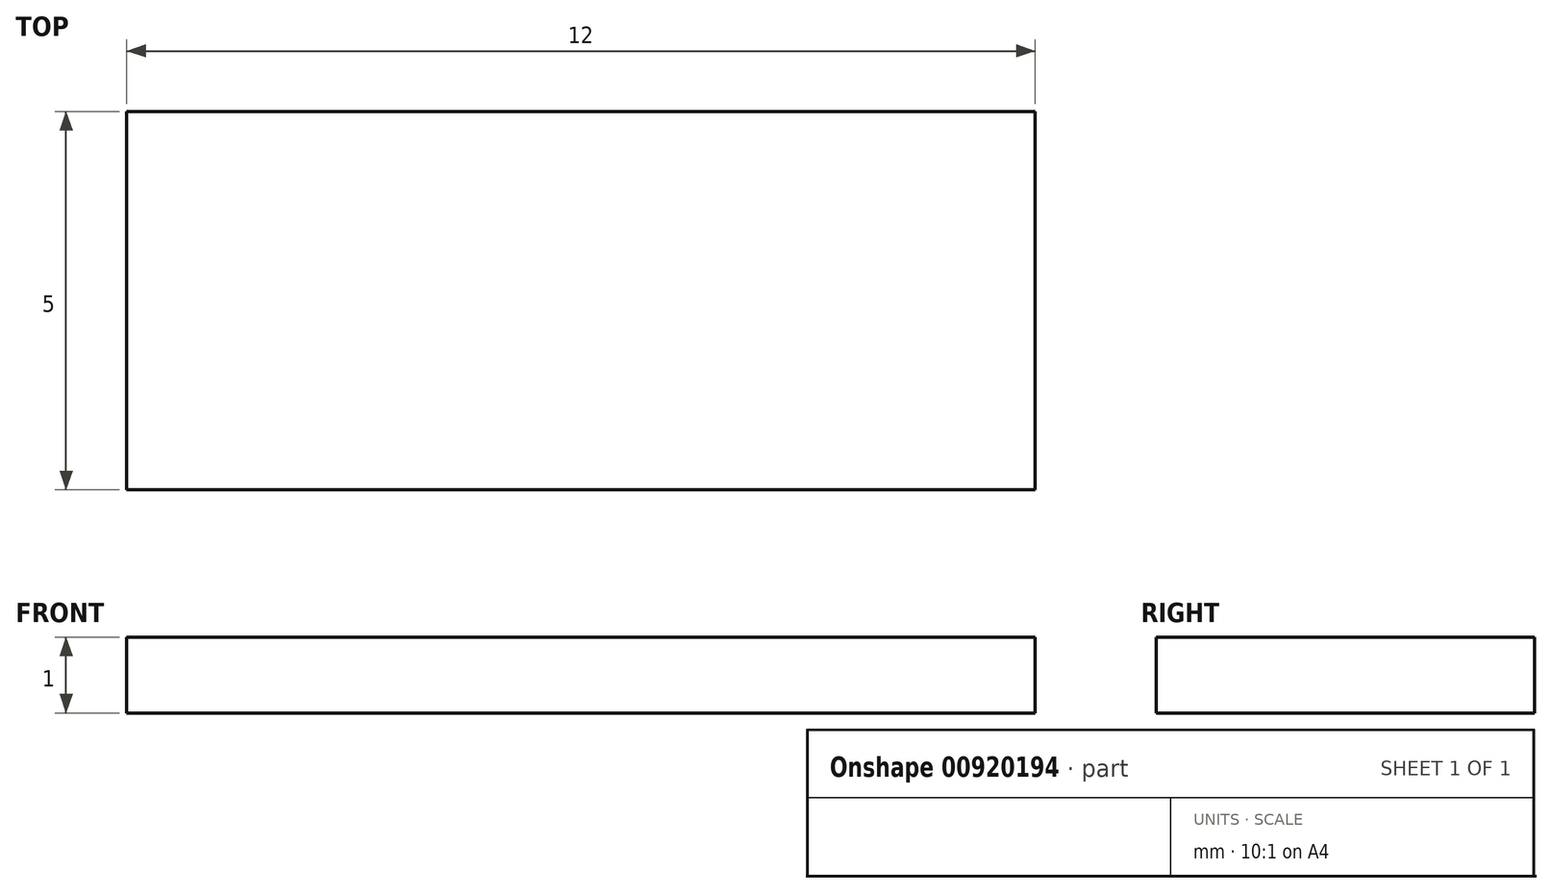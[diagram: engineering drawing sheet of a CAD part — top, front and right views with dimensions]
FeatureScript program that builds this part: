
annotation { "Feature Type Name" : "Feature", "Feature Type Description" : "" }
export const myFeature = defineFeature(function(context is Context, id is Id, definition is map)
    precondition{}
    {
        {
            var Q0;
            Q0=qCreatedBy(makeId("Top.planeOp"),FACE);
            var sketch = newSketch(context, id + "F0", { "sketchPlane" : qUnion([Q0])});
            skLineSegment(sketch, "E0.bottom", {"start": v(0, 0) * mm, "end": v(12, 0) * mm});
            skLineSegment(sketch, "E0.top", {"start": v(0, -5) * mm, "end": v(12, -5) * mm});
            skLineSegment(sketch, "E0.left", {"start": v(0, 0) * mm, "end": v(0, -5) * mm});
            skLineSegment(sketch, "E0.right", {"start": v(12, 0) * mm, "end": v(12, -5) * mm});
            skSolve(sketch);
        }
        {
            var Q0;
            Q0=makeQuery(id+"F0.imprint","IMPRINT",FACE,{"disambiguationData":[TD([[makeQuery(id+"F0.imprint","IMPRINT",EDGE,{"derivedFrom":sQuery(id+"F0.wireOp",EDGE,"E0.bottom")}),-1.0]])]});
            extrude(context, id + "F1", {"entities" : qUnion([Q0]), "depth" : 1 * mm, "offsetDistance" : 25 * mm});
        }
    });
